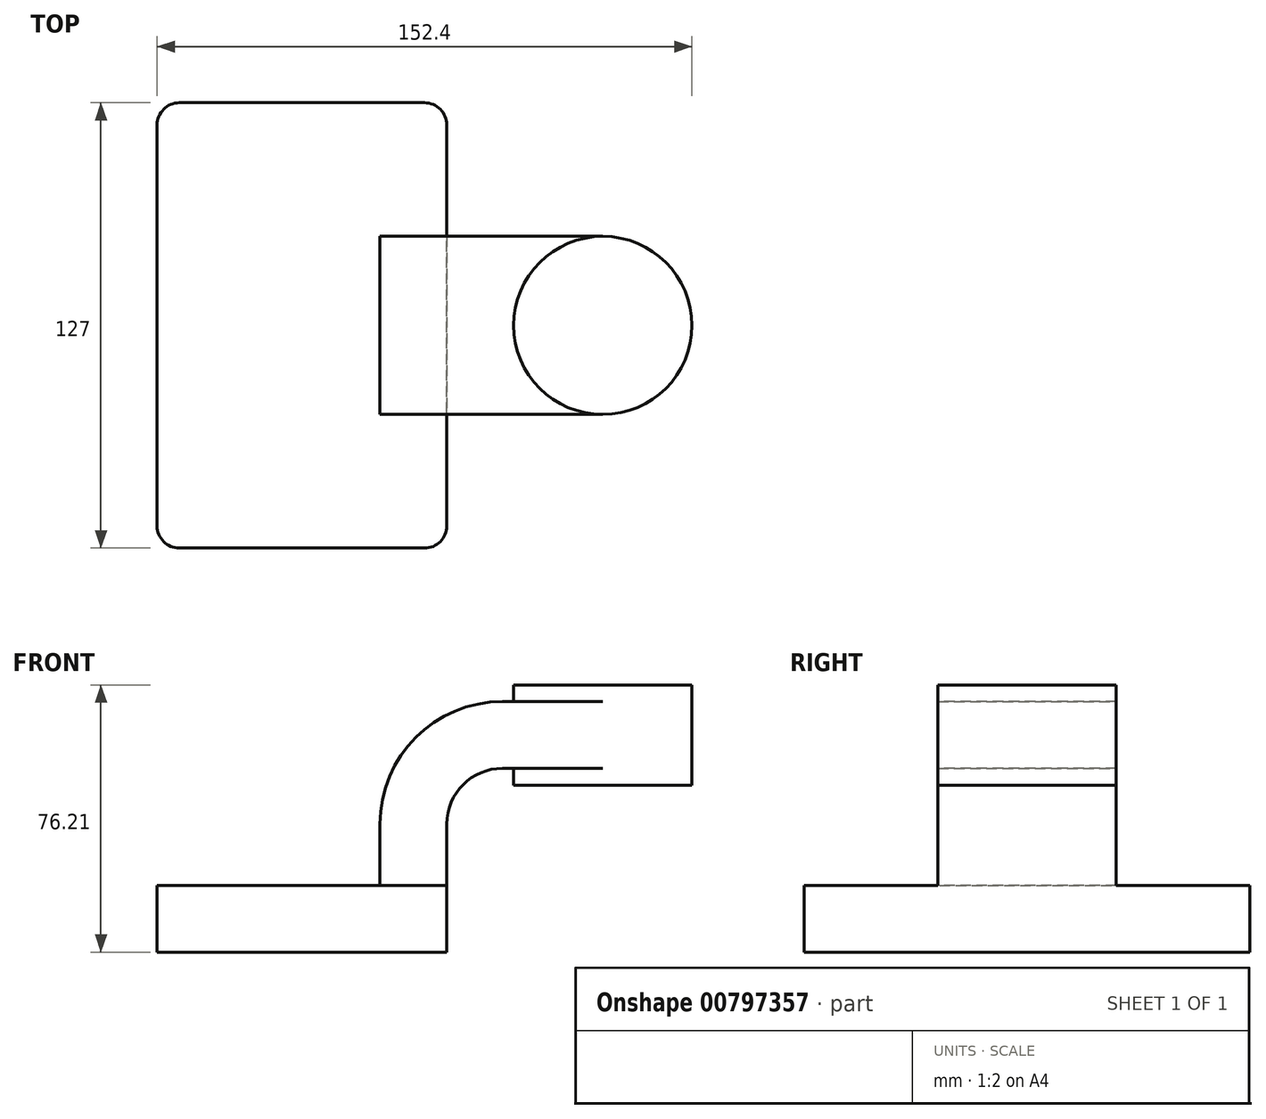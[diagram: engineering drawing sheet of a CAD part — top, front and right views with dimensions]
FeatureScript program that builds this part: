
annotation { "Feature Type Name" : "Feature", "Feature Type Description" : "" }
export const myFeature = defineFeature(function(context is Context, id is Id, definition is map)
    precondition{}
    {
        {
            var Q0;
            Q0=qCreatedBy(makeId("Front.planeOp"),FACE);
            var sketch = newSketch(context, id + "F0", { "sketchPlane" : qUnion([Q0])});
            skLineSegment(sketch, "E0.bottom", {"start": v(-41.28, -9.52) * mm, "end": v(41.28, -9.52) * mm});
            skLineSegment(sketch, "E0.top", {"start": v(-41.28, 9.53) * mm, "end": v(41.28, 9.53) * mm});
            skLineSegment(sketch, "E0.left", {"start": v(-41.28, -9.52) * mm, "end": v(-41.28, 9.53) * mm});
            skLineSegment(sketch, "E0.right", {"start": v(41.28, -9.52) * mm, "end": v(41.28, 9.53) * mm});
            skPoint(sketch, "E0.middle", {"position": v(0, 0) * mm});
            skLineSegment(sketch, "E1.bottom", {"start": v(60.32, 38.1) * mm, "end": v(111.12, 38.1) * mm});
            skLineSegment(sketch, "E1.top", {"start": v(60.32, 66.67) * mm, "end": v(111.12, 66.67) * mm});
            skLineSegment(sketch, "E1.left", {"start": v(60.32, 38.1) * mm, "end": v(60.32, 66.68) * mm});
            skLineSegment(sketch, "E1.right", {"start": v(111.12, 38.1) * mm, "end": v(111.12, 66.68) * mm});
            skPoint(sketch, "E1.middle", {"position": v(85.72, 52.39) * mm});
            skLineSegment(sketch, "E2", {"start": v(41.27, 9.53) * mm, "end": v(41.27, 27) * mm});
            skArc(sketch, "E3", {"start": v(41.27, 27) * mm, "mid": v(45.92, 38.23) * mm, "end": v(57.15, 42.88) * mm});
            skArc(sketch, "E4.1", {"start": v(22.22, 27) * mm, "mid": v(32.45, 51.7) * mm, "end": v(57.15, 61.93) * mm});
            skLineSegment(sketch, "E4.2", {"start": v(22.22, 9.53) * mm, "end": v(22.22, 27) * mm});
            skLineSegment(sketch, "E5", {"start": v(57.15, 61.93) * mm, "end": v(85.72, 61.93) * mm});
            skLineSegment(sketch, "E6", {"start": v(57.15, 42.88) * mm, "end": v(85.72, 42.88) * mm});
            skLineSegment(sketch, "E7", {"start": v(85.72, 66.68) * mm, "end": v(85.72, 38.1) * mm});
            skFitSpline(sketch, "E8", {"points": [v(-41.28, 9.53) * mm, v(57.15, 61.93) * mm], "startDerivative": vector(-1.98, 124.35) * mm, "endDerivative": vector(105.93, -0.56) * mm});
            skSolve(sketch);
        }
        {
            var Q0;
            Q0=makeQuery(id+"F0.imprint","IMPRINT",FACE,{"disambiguationData":[TD([[makeQuery(id+"F0.imprint","IMPRINT",EDGE,{"derivedFrom":sQuery(id+"F0.wireOp",EDGE,"E0.bottom")}),1.0]])]});
            extrude(context, id + "F1", {"entities" : qUnion([Q0]), "endBound" : BoundingType.SYMMETRIC, "depth" : 127 * mm, "offsetDistance" : 25.4 * mm});
        }
        {
            var Q0;
            {var subQ1=sQuery(id+"F0.wireOp",EDGE,"E2");Q0=makeQuery(id+"F0.imprint","IMPRINT",FACE,{"disambiguationData":[TD([[makeQuery(id+"F0.imprint","IMPRINT",EDGE,{"derivedFrom":subQ1}),1.0]])]});}
            var Q1;
            {var subQ0=sQuery(id+"F0.wireOp",EDGE,"E6");var subQ1=sQuery(id+"F0.wireOp",EDGE,"E1.left");var subQ2=makeQuery(id+"F0.imprint","INTERSECT",VERTEX,{"derivedFrom":[subQ1,subQ0]});Q1=makeQuery(id+"F0.imprint","IMPRINT",FACE,{"disambiguationData":[TD([[makeQuery(id+"F0.imprint","IMPRINT",EDGE,{"disambiguationData":[TD([[subQ2,-1.0]])],"derivedFrom":subQ1}),-1.0]])]});}
            extrude(context, id + "F2", {"entities" : qUnion([Q0, Q1]), "operationType" : NewBodyOperationType.ADD, "endBound" : BoundingType.SYMMETRIC, "oppositeDirection" : true, "depth" : 50.8 * mm, "offsetDistance" : 25.4 * mm});
        }
        {
            var Q0;
            Q0=makeQuery(id+"F0.imprint","IMPRINT",FACE,{"disambiguationData":[TD([[makeQuery(id+"F0.imprint","IMPRINT",EDGE,{"derivedFrom":sQuery(id+"F0.wireOp",EDGE,"E4.1")}),1.0]])]});
            extrude(context, id + "F3", {"entities" : qUnion([Q0]), "operationType" : NewBodyOperationType.ADD, "endBound" : BoundingType.SYMMETRIC, "depth" : 15.88 * mm, "offsetDistance" : 25.4 * mm});
        }
        {
            var Q0;
            {var subQ0=sQuery(id+"F0.wireOp",EDGE,"E1.right");Q0=makeQuery(id+"F0.imprint","IMPRINT",FACE,{"disambiguationData":[TD([[makeQuery(id+"F0.imprint","IMPRINT",EDGE,{"derivedFrom":subQ0}),1.0]])]});}
            var Q1;
            Q1=sQuery(id+"F0.wireOp",EDGE,"E7");
            revolve(context, id + "F4", {"operationType" : NewBodyOperationType.ADD, "surfaceOperationType" : NewSurfaceOperationType.NEW, "entities" : qUnion([Q0]), "axis" : qUnion([Q1]), "revolveType" : RevolveType.FULL});
        }
        {
            var Q0;
            Q0=makeQuery(id+"F1.opExtrude","CAP_EDGE",EDGE,{"disambiguationData":[OSD([sQuery(id+"F0.wireOp",EDGE,"E0.left")])],"isStart":false});
            var Q1;
            Q1=makeQuery(id+"F1.opExtrude","CAP_EDGE",EDGE,{"disambiguationData":[OSD([sQuery(id+"F0.wireOp",EDGE,"E0.right")])],"isStart":false});
            var Q2;
            Q2=makeQuery(id+"F1.opExtrude","CAP_EDGE",EDGE,{"disambiguationData":[OSD([sQuery(id+"F0.wireOp",EDGE,"E0.right")])],"isStart":true});
            var Q3;
            Q3=makeQuery(id+"F1.opExtrude","CAP_EDGE",EDGE,{"disambiguationData":[OSD([sQuery(id+"F0.wireOp",EDGE,"E0.left")])],"isStart":true});
            fillet(context, id + "F5", {"entities" : qUnion([Q0, Q1, Q2, Q3]), "radius" : 6.35 * mm, "tangentPropagation" : true, "allowEdgeOverflow" : false});
        }
    });
